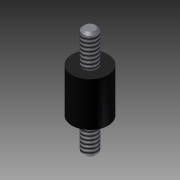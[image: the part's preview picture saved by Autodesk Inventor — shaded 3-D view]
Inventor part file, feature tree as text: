
AUTODESK INVENTOR PART (.ipt)
format: ipt  version: 2013 (Build 170138000, 138)  size: 86,528 bytes
history: native  units: mm (DEFAULTED — no unit token found)
features: thread x2, imported_body x1
ambient origin geometry x8: Origin, YZ Plane, XZ Plane, XY Plane, X Axis, Y Axis, Z Axis, Center Point
bodies: Solid1 (feature_tree)
feature tree (3):
  imported_body  "Base1"
  thread  "Thread1"  [1 undecoded]
  thread  "Thread2"  [1 undecoded]
note: 2 required parameter values undecoded (feature->parameter linkage not recoverable at this tier; creation-order binding heuristic only, values carry confidence <= 0.55)
